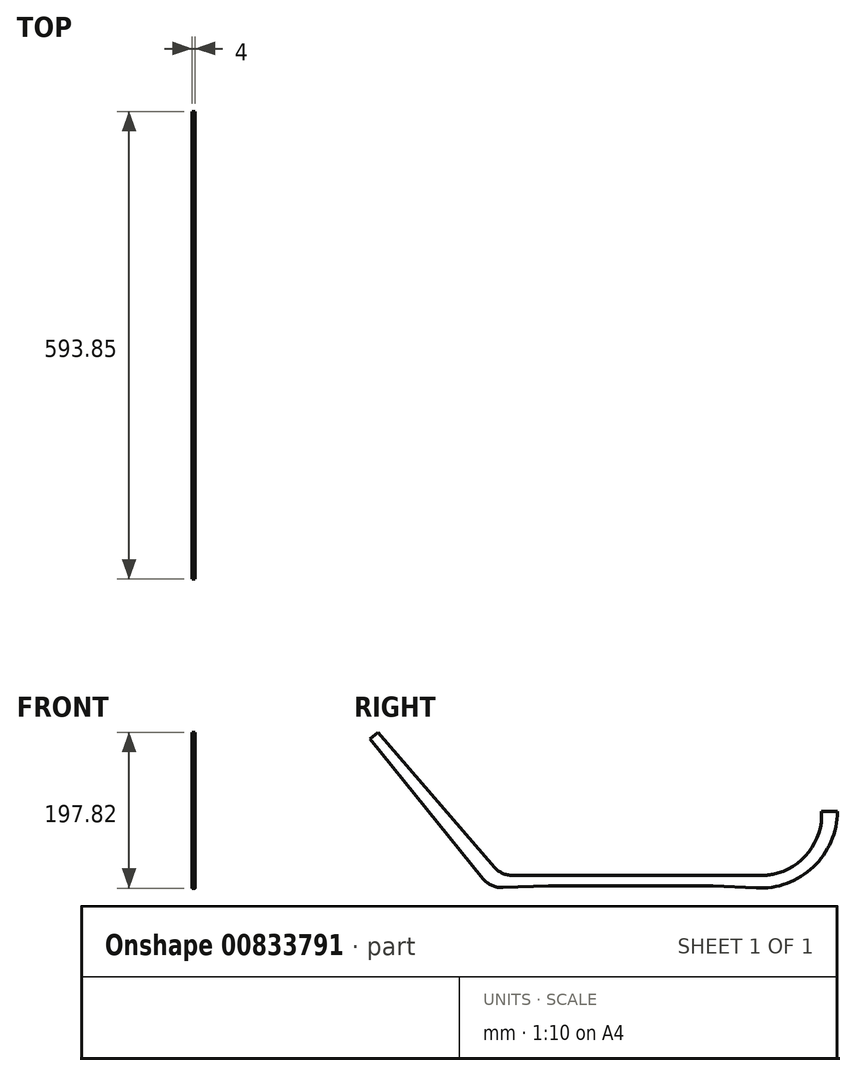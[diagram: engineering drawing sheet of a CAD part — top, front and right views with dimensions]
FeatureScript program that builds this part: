
annotation { "Feature Type Name" : "Feature", "Feature Type Description" : "" }
export const myFeature = defineFeature(function(context is Context, id is Id, definition is map)
    precondition{}
    {
        {
            var Q0;
            Q0=qCreatedBy(makeId("Right.planeOp"),FACE);
            var sketch = newSketch(context, id + "F0", { "sketchPlane" : qUnion([Q0])});
            skLineSegment(sketch, "E0", {"start": v(-7.03, 8.69) * mm, "end": v(-151.04, 186.52) * mm});
            skLineSegment(sketch, "E1", {"start": v(-75.52, 93.26) * mm, "end": v(74.9, 215.06) * mm, "construction": true});
            skLineSegment(sketch, "E2.1", {"start": v(29.92, 13) * mm, "end": v(349.36, 13) * mm});
            skLineSegment(sketch, "E3", {"start": v(-140.93, 194.7) * mm, "end": v(-151.04, 186.52) * mm});
            skLineSegment(sketch, "E4", {"start": v(-140.93, 194.7) * mm, "end": v(7.23, 23.38) * mm});
            skLineSegment(sketch, "E5", {"start": v(18.09, -2.38) * mm, "end": v(76.06, -0.08) * mm});
            skLineSegment(sketch, "E6", {"start": v(16.2, 13) * mm, "end": v(2.43, -3) * mm, "construction": true});
            skLineSegment(sketch, "E7.trimOffspring", {"start": v(80.02, 0) * mm, "end": v(275, 0) * mm});
            skPoint(sketch, "E8.start.orphan", {"position": v(0, 0) * mm});
            skPoint(sketch, "E9.orphan", {"position": v(6.2, 13) * mm});
            skPoint(sketch, "E10.visualSharp", {"position": v(16.2, 13) * mm});
            skArc(sketch, "E10.filletArc", {"start": v(7.23, 23.38) * mm, "mid": v(17.44, 15.72) * mm, "end": v(29.92, 13) * mm});
            skPoint(sketch, "E11.visualSharp", {"position": v(2.43, -3) * mm});
            skArc(sketch, "E11.filletArc", {"start": v(-7.03, 8.69) * mm, "mid": v(4.19, 0.11) * mm, "end": v(18.09, -2.38) * mm});
            skPoint(sketch, "E12.visualSharp", {"position": v(78.04, 0) * mm});
            skCircle(sketch, "E13", {"center": v(562.53, 42.62) * mm, "radius": 100 * mm});
            skLineSegment(sketch, "E14", {"start": v(562.53, 42.62) * mm, "end": v(562.53, -57.38) * mm, "construction": true});
            skArc(sketch, "E15.filletArc", {"start": v(80.02, 0) * mm, "mid": v(78.04, -0.02) * mm, "end": v(76.06, -0.08) * mm});
            skLineSegment(sketch, "E16", {"start": v(285, -0.25) * mm, "end": v(340, -3) * mm});
            skArc(sketch, "E17", {"start": v(340, -3) * mm, "mid": v(412.23, 23.7) * mm, "end": v(442.81, 94.38) * mm});
            skPoint(sketch, "E18.orphan", {"position": v(340, 0) * mm});
            skPoint(sketch, "E19.visualSharp", {"position": v(280, 0) * mm});
            skArc(sketch, "E19.filletArc", {"start": v(285, -0.25) * mm, "mid": v(280, -0.06) * mm, "end": v(275, 0) * mm});
            skArc(sketch, "E20.0", {"start": v(349.36, 13) * mm, "mid": v(355.04, 13.5) * mm, "end": v(360.67, 14.41) * mm});
            skLineSegment(sketch, "E21", {"start": v(442.81, 94.38) * mm, "end": v(426.81, 94.45) * mm});
            skArc(sketch, "E22", {"start": v(360.67, 14.41) * mm, "mid": v(406.64, 42.86) * mm, "end": v(422.81, 94.45) * mm});
            skLineSegment(sketch, "E23", {"start": v(422.81, 94.45) * mm, "end": v(426.81, 94.45) * mm});
            skSolve(sketch);
        }
        {
            var Q0;
            {var subQ4=sQuery(id+"F0.wireOp",EDGE,"E2.0");Q0=makeQuery(id+"F0.imprint","IMPRINT",FACE,{"disambiguationData":[TD([[makeQuery(id+"F0.imprint","IMPRINT",EDGE,{"derivedFrom":subQ4}),-1.0]])]});}
            var Q1;
            Q1=makeQuery(id+"F0.imprint","IMPRINT",FACE,{"disambiguationData":[TD([[makeQuery(id+"F0.imprint","IMPRINT",EDGE,{"derivedFrom":sQuery(id+"F0.wireOp",EDGE,"E0")}),-1.0]])]});
            extrude(context, id + "F1", {"entities" : qUnion([Q0, Q1]), "depth" : 4 * mm, "offsetDistance" : 25 * mm});
        }
    });
